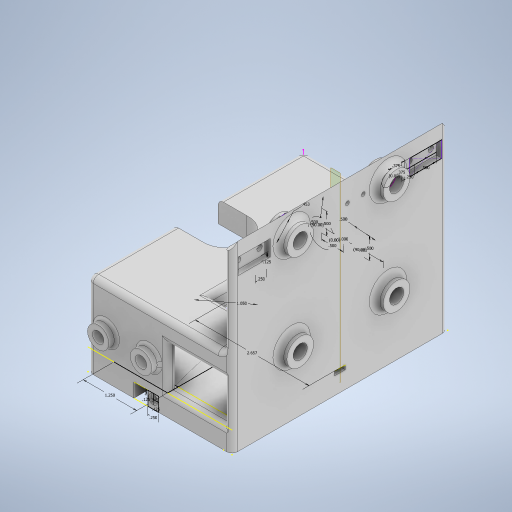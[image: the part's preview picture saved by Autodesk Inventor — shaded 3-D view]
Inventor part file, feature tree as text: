
AUTODESK INVENTOR PART (.ipt)
format: ipt  version: 2024.1 (Build 281209000, 209)  size: 987,136 bytes
history: native  units: in
note: dims shown in document units (in); Inventor stores cm internally (conversion verified against a paired STEP export)
features: extrude x22, sketch x15, hole x8, fillet x5, mirror x2, plane x1
ambient origin geometry x8: Origin, YZ Plane, XZ Plane, XY Plane, X Axis, Y Axis, Z Axis, Center Point
bodies: Solid1 (feature_tree)
feature tree (53):
  extrude  "Extrusion1"  Depth=3.3654in
  extrude  "Extrusion2"  Depth=0.375in
  extrude  "Extrusion3"  Depth=0.5in
  extrude  "Extrusion4"  Depth=4.5472in
  extrude  "Extrusion5"  Depth=0.25in
  extrude  "Extrusion6"  Depth=2.6575in
  hole  "Hole2"  [1 undecoded]
  extrude  "Extrusion7"  Depth=0.5in
  extrude  "Extrusion8"  Depth=1.5in
  extrude  "Extrusion9"  Depth=0.312in
  extrude  "Extrusion10"  Depth=0.312in
  hole  "Hole3"  [1 undecoded]
  extrude  "Extrusion11"  Depth=1.5in TaperAngle=0.0deg
  extrude  "Extrusion12"  Depth=1.125in
  hole  "Hole4"  [1 undecoded]
  sketch  "Sketch17"  dims[d34=1.4685in d35=0.0in d36=0.5in]
  extrude  "Extrusion13"  Depth=0.0625in
  hole  "Hole5"  [1 undecoded]
  plane  "Work Plane1"
  mirror  "Mirror1"
  extrude  "Extrusion14"  Depth=0.0625in
  fillet  "Fillet1"  [1 undecoded]
  extrude  "Extrusion15"  TaperAngle=0.0deg  [1 undecoded]
  fillet  "Fillet2"  Radius=0.625in
  hole  "Hole6"  [1 undecoded]
  mirror  "Mirror2"
  fillet  "Fillet3"  Radius=0.625in
  hole  "Hole7"  [1 undecoded]
  sketch  "Sketch22"  dims[d37=5.03in d38=0.0in d39=1.5in]
  extrude  "Extrusion16"  Depth=0.0625in TaperAngle=0.0deg
  fillet  "Fillet4"  Radius=0.36in
  sketch  "Sketch Driven Pattern1"  dims[d0=3.3654in d1=5.0299in]
  extrude  "Extrusion17"  Depth=0.0625in
  sketch  "Sketch24"  dims[d43=0.0in d44=0.312in]
  extrude  "Extrusion18"  Depth=0.0625in
  extrude  "Extrusion19"  Depth=0.0625in
  sketch  "Sketch26"  dims[d54=1.9685in d55=0.0in d56=1.5in d57=0.0in]
  extrude  "Extrusion20"  Depth=0.375in
  hole  "Hole8"  [1 undecoded]
  fillet  "Fillet5"  Radius=0.25in
  extrude  "Extrusion21"  Depth=0.5in
  sketch  "Sketch28"  dims[d61=1.49in d62=2.25in d63=2.25in d64=90.0deg d65=2.25in d66=90.0deg d67=0.332in d68=0.375in d69=0.119in d70=0.25in d71=0.5635in d72=0.375in d73=0.0in d74=0.0in d75=0.0in d76=0.625in d77=0.625in d78=0.625in d79=0.625in d80=0.2in d81=0.0in d82=0.36in d83=1.125in d84=0.185in d85=0.37in d86=0.09in d87=0.375in d88=0.119in d89=0.25in d90=0.5635in d91=0.375in d92=0.0in d93=0.375in d94=0.0in d95=0.25in d96=0.5in d97=0.375in d98=0.125in d99=0.0in d100=0.129in d101=0.198in d102=0.225in d103=0.188in d104=0.5635in d105=0.375in d106=0.0in d107=0.125in d108=0.125in d109=1.0in d110=1.0in d111=0.5in d112=1.5in d113=0.0in d114=0.931in d115=0.5in d116=1.0in d117=0.0in d120=0.1875in d121=0.0in d122=0.0625in d123=0.266in d124=0.75in d125=0.438in d126=0.25in d127=0.5635in d128=0.25in d129=0.0in d130=0.5in d131=90.0deg d132=0.5in d133=90.0deg d134=0.5in d135=0.5in d136=0.0625in d137=1.0in d138=0.5in d139=0.5in d140=90.0deg d141=0.5in d142=1.0in d143=180.0deg d144=1.0in d145=90.0deg d146=1.0in d147=0.266in d148=0.75in d149=0.438in d150=0.25in d151=0.5635in d152=1.0in d153=0.8108in d154=0.4532in d155=0.125in d156=0.0in d157=0.0312in d158=0.325in d159=0.1329in d160=0.3516in d161=0.1329in d162=0.3516in d163=0.448in d164=0.0in d165=0.647in d166=0.0in d167=0.325in d168=0.325in d169=0.25in d170=0.25in d171=0.5in d172=0.0in d173=0.25in d174=0.125in d175=0.0in d176=0.125in d177=0.129in d178=0.75in d179=0.219in d180=0.0625in d181=0.5635in d182=1.0in d183=0.8108in d184=0.125in d185=1.075in d186=0.325in d187=0.575in d188=0.5in d189=0.0in d190=0.25in d191=0.125in d192=0.125in d193=0.125in d194=0.0in d195=0.129in d196=0.224in d197=0.219in d198=0.0625in d199=0.5635in d200=1.0in d201=0.8108in]
  extrude  "Extrusion22"  Depth=0.375in
  hole  "Hole9"  [1 undecoded]
  sketch  "Sketch7"  dims[d3=45.0deg d4=0.375in]
  sketch  "Sketch9"  dims[d5=0.5in d6=0.0in d23=2.8543in]
  sketch  "Sketch10"  dims[d24=5.315in d25=4.5472in]
  sketch  "Sketch11"  dims[d26=0.1in d27=0.0in d28=0.25in]
  sketch  "Sketch12"  dims[d29=0.1in d30=0.0in d31=2.6575in]
  sketch  "Sketch15"  dims[d32=1.05in d33=1.25in]
  sketch  "Sketch23"  dims[d40=1.0in d41=0.0in d42=0.312in]
  sketch  "Sketch25"  dims[d45=0.196in d46=0.75in d47=0.385in d48=0.25in d49=0.5635in d50=1.378in d51=0.0in d52=1.4685in d53=0.0in]
  sketch  "Sketch27"  dims[d58=3.75in d59=0.0in d60=1.125in]
note: 10 required parameter values undecoded (feature->parameter linkage not recoverable at this tier; creation-order binding heuristic only, values carry confidence <= 0.55)
